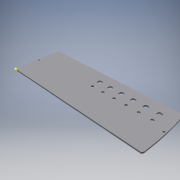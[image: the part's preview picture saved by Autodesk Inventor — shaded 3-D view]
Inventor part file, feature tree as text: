
AUTODESK INVENTOR PART (.ipt)
format: ipt  version: 2018 (Build 220112000, 112)  size: 184,320 bytes
history: native  units: mm
features: sketch x5, extrude x3, hole x1
ambient origin geometry x8: Origin, YZ Plane, XZ Plane, XY Plane, X Axis, Y Axis, Z Axis, Center Point
bodies: Volumenkörper1 (feature_tree)
feature tree (9):
  extrude  "Extrusion1"  Depth=85.0mm
  hole  "Bohrung1"  [1 undecoded]
  extrude  "Extrusion2"  Depth=2.0mm
  sketch  "Sketch7"  dims[d7=452.5625mm d8=452.5625mm]
  extrude  "Extrusion6"  Depth=452.5625mm
  sketch  "Skizze1"  dims[d0=85.0mm d1=242.0mm]
  sketch  "Skizze2"  dims[d2=2.0mm d3=2.0mm]
  sketch  "Skizze3"  dims[d4=2.0mm d5=905.125mm d6=905.125mm]
  sketch  "Sketch9"  dims[d9=2.5mm d10=0.0mm d11=42.5mm d12=42.5mm d13=235.8mm d14=117.9mm d15=117.9mm d16=3.3mm d17=6.0mm d18=4.0mm d19=2.0mm d20=90.0deg d21=8.0mm d22=20.594885mm d23=9.599311mm d24=9.599311mm d25=2.5mm d26=2.5mm d27=5.0mm d28=0.0mm d96=8.1mm d97=20.0mm d98=20.0mm d99=7.1mm d100=4.05mm d101=60.0mm d103=20.0mm d104=10.0mm d106=10.0mm d108=15.0mm d109=4.8mm d110=60.0mm d112=20.0mm d113=10.0mm d115=10.0mm d117=3.0mm d118=0.0mm]
note: 1 required parameter value undecoded (feature->parameter linkage not recoverable at this tier; creation-order binding heuristic only, values carry confidence <= 0.55)
